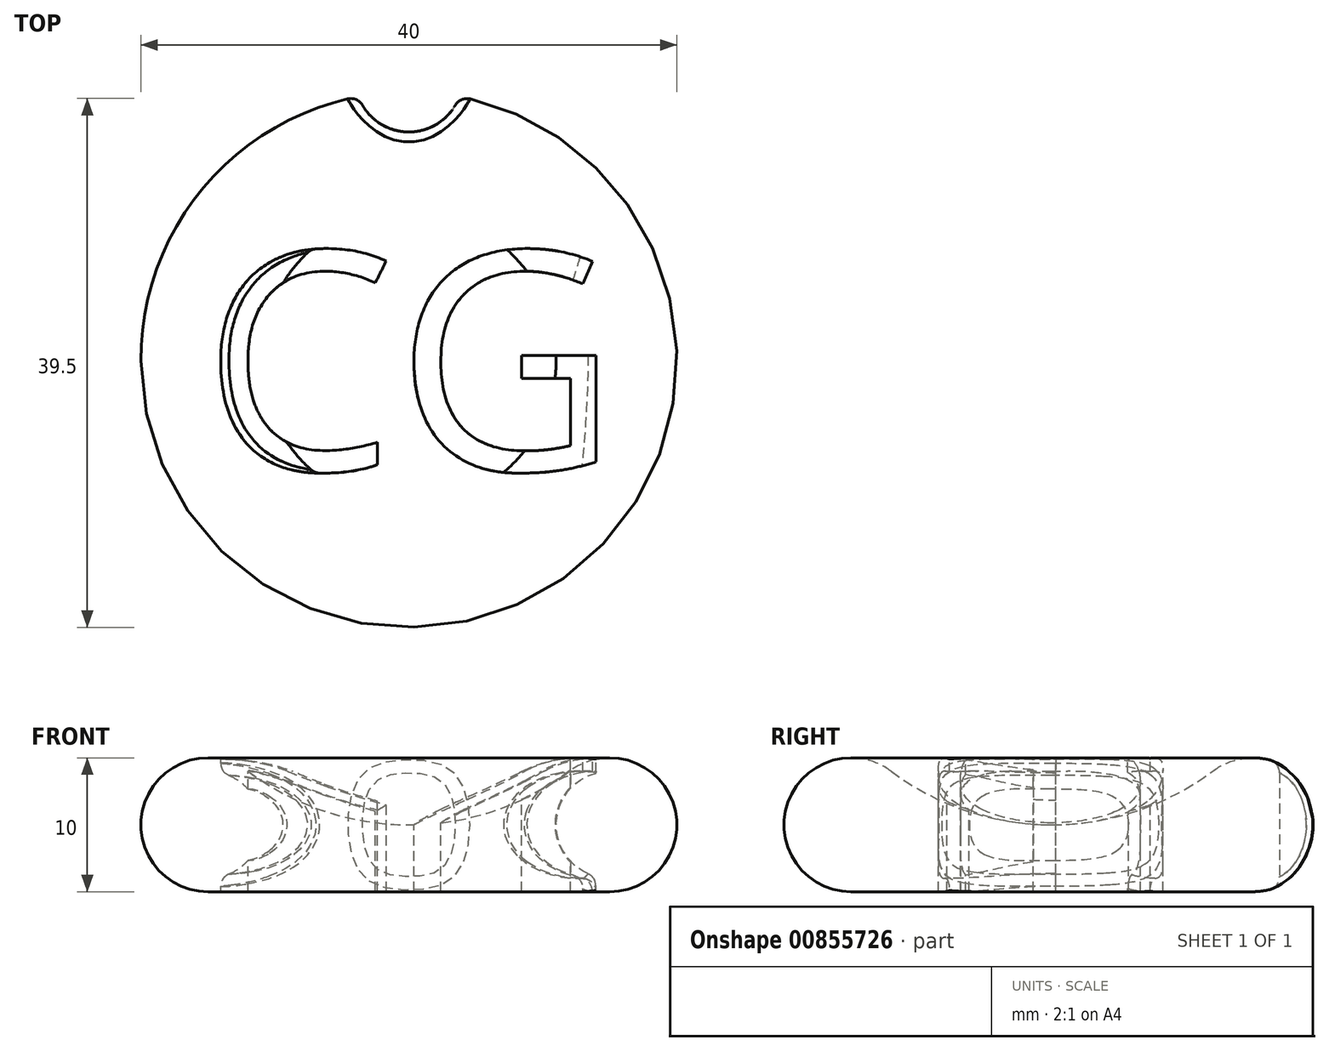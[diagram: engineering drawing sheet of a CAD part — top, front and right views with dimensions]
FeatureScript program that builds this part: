
annotation { "Feature Type Name" : "Feature", "Feature Type Description" : "" }
export const myFeature = defineFeature(function(context is Context, id is Id, definition is map)
    precondition{}
    {
        {
            var Q0;
            Q0=qCreatedBy(makeId("Front.planeOp"),FACE);
            var sketch = newSketch(context, id + "F0", { "sketchPlane" : qUnion([Q0])});
            skArc(sketch, "E0", {"start": v(-12, 9) * mm, "mid": v(-19.74, 6.58) * mm, "end": v(-15, 0) * mm});
            skArc(sketch, "E1", {"start": v(-12, 9) * mm, "mid": v(-6.32, 6.03) * mm, "end": v(0, 5) * mm});
            skLineSegment(sketch, "E2", {"start": v(0, 0) * mm, "end": v(-15, 0) * mm});
            skLineSegment(sketch, "E3", {"start": v(0, 0) * mm, "end": v(0, 5) * mm});
            skSolve(sketch);
        }
        {
            var Q0;
            Q0=makeQuery(id+"F0.imprint","IMPRINT",FACE,{"disambiguationData":[TD([[makeQuery(id+"F0.imprint","IMPRINT",EDGE,{"derivedFrom":sQuery(id+"F0.wireOp",EDGE,"E0")}),1.0]])]});
            var Q1;
            Q1=sQuery(id+"F0.wireOp",EDGE,"E3");
            revolve(context, id + "F1", {"surfaceOperationType" : NewSurfaceOperationType.NEW, "entities" : qUnion([Q0]), "axis" : qUnion([Q1]), "revolveType" : RevolveType.FULL});
        }
        {
            var Q0;
            Q0=qCreatedBy(makeId("Top.planeOp"),FACE);
            cPlane(context, id + "F2", {"entities" : qUnion([Q0]), "cplaneType" : CPlaneType.OFFSET, "offset" : 10 * mm, "width" : 150 * mm, "height" : 150 * mm});
        }
        {
            var Q0;
            Q0=qCreatedBy(id+"F2.planeOp",FACE);
            var sketch = newSketch(context, id + "F3", { "sketchPlane" : qUnion([Q0])});
            skText(sketch, "E4", { "text": "CG", "fontName": "OpenSans-Regular.ttf"});
            const initialGuessF3  = {"E4": [-0.01544, -0.00826, 1, 0, 0.01646]};
            skSetInitialGuess(sketch, initialGuessF3);
            skSolve(sketch);
        }
        {
            var Q0;
            Q0 = qSketchRegion(id + "F3", true);
            extrude(context, id + "F4", {"entities" : qUnion([Q0]), "operationType" : NewBodyOperationType.REMOVE, "oppositeDirection" : true, "depth" : 25 * mm, "offsetDistance" : 25 * mm});
        }
        {
            var Q0;
            Q0=qCreatedBy(makeId("Front.planeOp"),FACE);
            var sketch = newSketch(context, id + "F5", { "sketchPlane" : qUnion([Q0])});
            skCircle(sketch, "E5", {"center": v(-15, 5) * mm, "radius": 4 * mm});
            skSolve(sketch);
        }
        {
            var Q0;
            Q0 = qSketchRegion(id + "F5", true);
            var Q1;
            Q1=sQuery(id+"F0.wireOp",EDGE,"E3");
            revolve(context, id + "F6", {"operationType" : NewBodyOperationType.ADD, "surfaceOperationType" : NewSurfaceOperationType.NEW, "entities" : qUnion([Q0]), "axis" : qUnion([Q1]), "revolveType" : RevolveType.FULL});
        }
        {
            var Q0;
            Q0=qCreatedBy(makeId("Top.planeOp"),FACE);
            var sketch = newSketch(context, id + "F7", { "sketchPlane" : qUnion([Q0])});
            skCircle(sketch, "E6", {"center": v(0, 21) * mm, "radius": 4 * mm});
            skSolve(sketch);
        }
        {
            var Q0;
            Q0 = qSketchRegion(id + "F7", true);
            extrude(context, id + "F8", {"entities" : qUnion([Q0]), "operationType" : NewBodyOperationType.REMOVE, "depth" : 25 * mm, "offsetDistance" : 25 * mm});
        }
        {
            var Q0;
            Q0=makeQuery(id+"F8.boolean.opBoolean","INTERSECT",EDGE,{"derivedFrom":[makeQuery(id+"F4.boolean.opBoolean","SPLIT",FACE,{"disambiguationData":[TD([makeQuery(id+"F1.opRevolve","SWEPT_FACE",FACE,{"disambiguationData":[OSD([sQuery(id+"F0.wireOp",EDGE,"E2")])]})])],"derivedFrom":makeQuery(id+"F1.opRevolve","SWEPT_FACE",FACE,{"disambiguationData":[OSD([sQuery(id+"F0.wireOp",EDGE,"E0")])]})}),makeQuery(id+"F8.opExtrude","SWEPT_FACE",FACE,{"disambiguationData":[OSD([sQuery(id+"F7.wireOp",EDGE,"E6")])]})]});
            fillet(context, id + "F9", {"entities" : qUnion([Q0]), "radius" : 1 * mm, "tangentPropagation" : true, "allowEdgeOverflow" : false});
        }
        {
            var Q0;
            Q0=makeQuery(id+"F6.boolean.opBoolean","INTERSECT",EDGE,{"disambiguationData":[OD(0.0)],"derivedFrom":[makeQuery(id+"F4.boolean.opBoolean","COPY",FACE,{"derivedFrom":makeQuery(id+"F4.opExtrude","SWEPT_FACE",FACE,{"disambiguationData":[OSD([sQuery(id+"F3.wireOp",EDGE,"E4.sketch_text.stroke-16")])]})}),makeQuery(id+"F6.opRevolve","SWEPT_FACE",FACE,{"disambiguationData":[OSD([sQuery(id+"F5.wireOp",EDGE,"E5")])]})]});
            var Q1;
            Q1=makeQuery(id+"F6.boolean.opBoolean","INTERSECT",EDGE,{"disambiguationData":[OD(0.0)],"derivedFrom":[makeQuery(id+"F4.boolean.opBoolean","COPY",FACE,{"derivedFrom":makeQuery(id+"F4.opExtrude","SWEPT_FACE",FACE,{"disambiguationData":[OSD([sQuery(id+"F3.wireOp",EDGE,"E4.sketch_text.stroke-25")])]})}),makeQuery(id+"F6.opRevolve","SWEPT_FACE",FACE,{"disambiguationData":[OSD([sQuery(id+"F5.wireOp",EDGE,"E5")])]})]});
            var Q2;
            Q2=makeQuery(id+"F6.boolean.opBoolean","INTERSECT",EDGE,{"disambiguationData":[OD(1.0)],"derivedFrom":[makeQuery(id+"F4.boolean.opBoolean","COPY",FACE,{"derivedFrom":makeQuery(id+"F4.opExtrude","SWEPT_FACE",FACE,{"disambiguationData":[OSD([sQuery(id+"F3.wireOp",EDGE,"E4.sketch_text.stroke-10")])]})}),makeQuery(id+"F6.opRevolve","SWEPT_FACE",FACE,{"disambiguationData":[OSD([sQuery(id+"F5.wireOp",EDGE,"E5")])]})]});
            var Q3;
            Q3=makeQuery(id+"F6.boolean.opBoolean","INTERSECT",EDGE,{"disambiguationData":[OD(1.0)],"derivedFrom":[makeQuery(id+"F4.boolean.opBoolean","COPY",FACE,{"derivedFrom":makeQuery(id+"F4.opExtrude","SWEPT_FACE",FACE,{"disambiguationData":[OSD([sQuery(id+"F3.wireOp",EDGE,"E4.sketch_text.stroke-9")])]})}),makeQuery(id+"F6.opRevolve","SWEPT_FACE",FACE,{"disambiguationData":[OSD([sQuery(id+"F5.wireOp",EDGE,"E5")])]})]});
            var Q4;
            Q4=makeQuery(id+"F6.boolean.opBoolean","INTERSECT",EDGE,{"disambiguationData":[OD(1.0)],"derivedFrom":[makeQuery(id+"F4.boolean.opBoolean","COPY",FACE,{"derivedFrom":makeQuery(id+"F4.opExtrude","SWEPT_FACE",FACE,{"disambiguationData":[OSD([sQuery(id+"F3.wireOp",EDGE,"E4.sketch_text.stroke-8")])]})}),makeQuery(id+"F6.opRevolve","SWEPT_FACE",FACE,{"disambiguationData":[OSD([sQuery(id+"F5.wireOp",EDGE,"E5")])]})]});
            fillet(context, id + "F10", {"entities" : qUnion([Q0, Q1, Q2, Q3, Q4]), "radius" : 1 * mm, "tangentPropagation" : true, "allowEdgeOverflow" : false});
        }
    });
